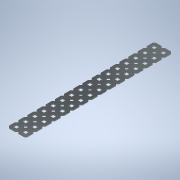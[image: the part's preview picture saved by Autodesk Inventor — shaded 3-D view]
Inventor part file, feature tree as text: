
AUTODESK INVENTOR PART (.ipt)
format: ipt  version: 2020 (Build 240168000, 168)  size: 2,255,872 bytes
history: native  units: mm (DEFAULTED — no unit token found)
features: other x125, extrude x125, plane x2, split x2, imported_body x1, pattern_linear x1, sketch x1
ambient origin geometry x8: Origin, YZ Plane, XZ Plane, XY Plane, X Axis, Y Axis, Z Axis, Center Point
bodies: Solid1 (feature_tree)
feature tree (257):
  imported_body  "Base1"
  pattern_linear  "Rectangular Pattern1"  Spacing1=0.0mm  [1 undecoded]
  plane  "Work Plane1"
  split  "Split1"
  plane  "Work Plane2"
  split  "Split2"
  sketch  "Sketch1"  dims[d1=1.1684mm d2=0.0mm d3=250.0mm d5=12.7mm d6=50.0mm d8=12.7mm d9=0.0mm d10=0.0mm d11=0.0mm d12=0.0mm d13=0.0mm d14=0.0mm d15=0.0mm d16=0.0mm d17=0.0mm d18=0.0mm d19=0.0mm d20=0.0mm d21=0.0mm d22=0.0mm d23=0.0mm d24=0.0mm d25=0.0mm d26=0.0mm d27=0.0mm d28=0.0mm d29=0.0mm d30=0.0mm d31=0.0mm d32=0.0mm d33=0.0mm d34=0.0mm d35=0.0mm d36=0.0mm d37=0.0mm d38=0.0mm d39=0.0mm d40=0.0mm d41=0.0mm d42=0.0mm d43=0.0mm d44=0.0mm d45=0.0mm d46=0.0mm d47=0.0mm d48=0.0mm d49=0.0mm d50=0.0mm d51=0.0mm d52=0.0mm d53=0.0mm d54=0.0mm d55=0.0mm d56=0.0mm d57=0.0mm d58=0.0mm d59=0.0mm d60=0.0mm d61=0.0mm d62=0.0mm d63=0.0mm d64=0.0mm d65=0.0mm d66=0.0mm d67=0.0mm d68=0.0mm d69=0.0mm d70=0.0mm d71=0.0mm d72=0.0mm d73=0.0mm d74=0.0mm d75=0.0mm d76=0.0mm d77=0.0mm d78=0.0mm d79=0.0mm d80=0.0mm d81=0.0mm d82=0.0mm d83=0.0mm d84=0.0mm d85=0.0mm d86=0.0mm d87=0.0mm d88=0.0mm d89=0.0mm d90=0.0mm d91=0.0mm d92=0.0mm d93=0.0mm d94=0.0mm d95=0.0mm d96=0.0mm d97=0.0mm d98=0.0mm d99=0.0mm d100=0.0mm d101=0.0mm d102=0.0mm d103=0.0mm d104=0.0mm d105=0.0mm d106=0.0mm d107=0.0mm d108=0.0mm d109=0.0mm d110=0.0mm d111=0.0mm d112=0.0mm d113=0.0mm d114=0.0mm d115=0.0mm d116=0.0mm d117=0.0mm d118=0.0mm d119=0.0mm d120=0.0mm d121=0.0mm d122=0.0mm d123=0.0mm d124=0.0mm d125=0.0mm d126=0.0mm d127=0.0mm d128=0.0mm d129=0.0mm d130=0.0mm d131=0.0mm d132=0.0mm d133=0.0mm d134=0.0mm d135=0.0mm d136=0.0mm d137=0.0mm d138=0.0mm d139=0.0mm d140=0.0mm d141=0.0mm d142=0.0mm d143=0.0mm d144=0.0mm d145=0.0mm d146=0.0mm d147=0.0mm d148=0.0mm d149=0.0mm d150=0.0mm d151=0.0mm d152=0.0mm d153=0.0mm d154=0.0mm d155=0.0mm d156=0.0mm d157=0.0mm d158=0.0mm d159=0.0mm d160=0.0mm d161=0.0mm d162=0.0mm d163=0.0mm d164=0.0mm d165=0.0mm d166=0.0mm d167=0.0mm d168=0.0mm d169=0.0mm d170=0.0mm d171=0.0mm d172=0.0mm d173=0.0mm d174=0.0mm d175=0.0mm d176=0.0mm d177=0.0mm d178=0.0mm d179=0.0mm d180=0.0mm d181=0.0mm d182=0.0mm d183=0.0mm d184=0.0mm d185=0.0mm d186=0.0mm d187=0.0mm d188=0.0mm d189=0.0mm d190=0.0mm d191=0.0mm d192=0.0mm d193=0.0mm d194=0.0mm d195=0.0mm d196=0.0mm d197=0.0mm d198=0.0mm d199=0.0mm d200=0.0mm d201=0.0mm d202=0.0mm d203=0.0mm d204=0.0mm d205=0.0mm d206=0.0mm d207=0.0mm d208=0.0mm d209=0.0mm d210=0.0mm d211=0.0mm d212=0.0mm d213=0.0mm d214=0.0mm d215=0.0mm d216=0.0mm d217=0.0mm d218=0.0mm d219=0.0mm d220=0.0mm d221=0.0mm d222=0.0mm d223=0.0mm d224=0.0mm d225=0.0mm d226=0.0mm d227=0.0mm d228=0.0mm d229=0.0mm d230=0.0mm d231=0.0mm d232=0.0mm d233=0.0mm d234=0.0mm d235=0.0mm d236=0.0mm d237=0.0mm d238=0.0mm d239=0.0mm d240=0.0mm d241=0.0mm d242=0.0mm d243=0.0mm d244=0.0mm d245=0.0mm d246=0.0mm d247=0.0mm d248=0.0mm d249=0.0mm d250=0.0mm d251=0.0mm d252=0.0mm d253=0.0mm d254=0.0mm d255=0.0mm d256=0.0mm d257=0.0mm d258=0.0mm]
  other  "Srf1"
  other  "Srf2"
  other  "Srf3"
  other  "Srf4"
  other  "Srf5"
  other  "Srf6"
  other  "Srf7"
  other  "Srf8"
  other  "Srf9"
  other  "Srf10"
  other  "Srf11"
  other  "Srf12"
  other  "Srf13"
  other  "Srf14"
  other  "Srf15"
  other  "Srf16"
  other  "Srf17"
  other  "Srf18"
  other  "Srf19"
  other  "Srf20"
  other  "Srf21"
  other  "Srf22"
  other  "Srf23"
  other  "Srf24"
  other  "Srf25"
  other  "Srf26"
  other  "Srf27"
  other  "Srf28"
  other  "Srf29"
  other  "Srf30"
  other  "Srf31"
  other  "Srf32"
  other  "Srf33"
  other  "Srf34"
  other  "Srf35"
  other  "Srf36"
  other  "Srf37"
  other  "Srf38"
  other  "Srf39"
  other  "Srf40"
  other  "Srf41"
  other  "Srf42"
  other  "Srf43"
  other  "Srf44"
  other  "Srf45"
  other  "Srf46"
  other  "Srf47"
  other  "Srf48"
  other  "Srf49"
  other  "Srf50"
  other  "Srf51"
  other  "Srf52"
  other  "Srf53"
  other  "Srf54"
  other  "Srf55"
  other  "Srf56"
  other  "Srf57"
  other  "Srf58"
  other  "Srf59"
  other  "Srf60"
  other  "Srf61"
  other  "Srf62"
  other  "Srf63"
  other  "Srf64"
  other  "Srf65"
  other  "Srf66"
  other  "Srf67"
  other  "Srf68"
  other  "Srf69"
  other  "Srf70"
  other  "Srf71"
  other  "Srf72"
  other  "Srf73"
  other  "Srf74"
  other  "Srf75"
  other  "Srf76"
  other  "Srf77"
  other  "Srf78"
  other  "Srf79"
  other  "Srf80"
  other  "Srf81"
  other  "Srf82"
  other  "Srf83"
  other  "Srf84"
  other  "Srf85"
  other  "Srf86"
  other  "Srf87"
  other  "Srf88"
  other  "Srf89"
  other  "Srf90"
  other  "Srf91"
  other  "Srf92"
  other  "Srf93"
  other  "Srf94"
  other  "Srf95"
  other  "Srf96"
  other  "Srf97"
  other  "Srf98"
  other  "Srf99"
  other  "Srf100"
  other  "Srf101"
  other  "Srf102"
  other  "Srf103"
  other  "Srf104"
  other  "Srf105"
  other  "Srf106"
  other  "Srf107"
  other  "Srf108"
  other  "Srf109"
  other  "Srf110"
  other  "Srf111"
  other  "Srf112"
  other  "Srf113"
  other  "Srf114"
  other  "Srf115"
  other  "Srf116"
  other  "Srf117"
  other  "Srf118"
  other  "Srf119"
  other  "Srf120"
  other  "Srf121"
  other  "Srf122"
  other  "Srf123"
  other  "Srf124"
  other  "Srf125"
  extrude  "ExtrusionSrf1"  Depth=250.0mm
  extrude  "ExtrusionSrf2"  Depth=12.7mm
  extrude  "ExtrusionSrf3"  Depth=50.0mm
  extrude  "ExtrusionSrf4"  TaperAngle=0.0deg  [1 undecoded]
  extrude  "ExtrusionSrf5"  TaperAngle=0.0deg  [1 undecoded]
  extrude  "ExtrusionSrf6"  TaperAngle=0.0deg  [1 undecoded]
  extrude  "ExtrusionSrf7"  TaperAngle=0.0deg  [1 undecoded]
  extrude  "ExtrusionSrf8"  TaperAngle=0.0deg  [1 undecoded]
  extrude  "ExtrusionSrf9"  TaperAngle=0.0deg  [1 undecoded]
  extrude  "ExtrusionSrf10"  TaperAngle=0.0deg  [1 undecoded]
  extrude  "ExtrusionSrf11"  TaperAngle=0.0deg  [1 undecoded]
  extrude  "ExtrusionSrf12"  TaperAngle=0.0deg  [1 undecoded]
  extrude  "ExtrusionSrf13"  TaperAngle=0.0deg  [1 undecoded]
  extrude  "ExtrusionSrf14"  TaperAngle=0.0deg  [1 undecoded]
  extrude  "ExtrusionSrf15"  TaperAngle=0.0deg  [1 undecoded]
  extrude  "ExtrusionSrf16"  TaperAngle=0.0deg  [1 undecoded]
  extrude  "ExtrusionSrf17"  TaperAngle=0.0deg  [1 undecoded]
  extrude  "ExtrusionSrf18"  TaperAngle=0.0deg  [1 undecoded]
  extrude  "ExtrusionSrf19"  TaperAngle=0.0deg  [1 undecoded]
  extrude  "ExtrusionSrf20"  TaperAngle=0.0deg  [1 undecoded]
  extrude  "ExtrusionSrf21"  TaperAngle=0.0deg  [1 undecoded]
  extrude  "ExtrusionSrf22"  TaperAngle=0.0deg  [1 undecoded]
  extrude  "ExtrusionSrf23"  TaperAngle=0.0deg  [1 undecoded]
  extrude  "ExtrusionSrf24"  TaperAngle=0.0deg  [1 undecoded]
  extrude  "ExtrusionSrf25"  TaperAngle=0.0deg  [1 undecoded]
  extrude  "ExtrusionSrf26"  TaperAngle=0.0deg  [1 undecoded]
  extrude  "ExtrusionSrf27"  TaperAngle=0.0deg  [1 undecoded]
  extrude  "ExtrusionSrf28"  TaperAngle=0.0deg  [1 undecoded]
  extrude  "ExtrusionSrf29"  TaperAngle=0.0deg  [1 undecoded]
  extrude  "ExtrusionSrf30"  TaperAngle=0.0deg  [1 undecoded]
  extrude  "ExtrusionSrf31"  TaperAngle=0.0deg  [1 undecoded]
  extrude  "ExtrusionSrf32"  TaperAngle=0.0deg  [1 undecoded]
  extrude  "ExtrusionSrf33"  TaperAngle=0.0deg  [1 undecoded]
  extrude  "ExtrusionSrf34"  TaperAngle=0.0deg  [1 undecoded]
  extrude  "ExtrusionSrf35"  TaperAngle=0.0deg  [1 undecoded]
  extrude  "ExtrusionSrf36"  TaperAngle=0.0deg  [1 undecoded]
  extrude  "ExtrusionSrf37"  TaperAngle=0.0deg  [1 undecoded]
  extrude  "ExtrusionSrf38"  TaperAngle=0.0deg  [1 undecoded]
  extrude  "ExtrusionSrf39"  TaperAngle=0.0deg  [1 undecoded]
  extrude  "ExtrusionSrf40"  TaperAngle=0.0deg  [1 undecoded]
  extrude  "ExtrusionSrf41"  TaperAngle=0.0deg  [1 undecoded]
  extrude  "ExtrusionSrf42"  TaperAngle=0.0deg  [1 undecoded]
  extrude  "ExtrusionSrf43"  TaperAngle=0.0deg  [1 undecoded]
  extrude  "ExtrusionSrf44"  TaperAngle=0.0deg  [1 undecoded]
  extrude  "ExtrusionSrf45"  TaperAngle=0.0deg  [1 undecoded]
  extrude  "ExtrusionSrf46"  TaperAngle=0.0deg  [1 undecoded]
  extrude  "ExtrusionSrf47"  TaperAngle=0.0deg  [1 undecoded]
  extrude  "ExtrusionSrf48"  TaperAngle=0.0deg  [1 undecoded]
  extrude  "ExtrusionSrf49"  TaperAngle=0.0deg  [1 undecoded]
  extrude  "ExtrusionSrf50"  TaperAngle=0.0deg  [1 undecoded]
  extrude  "ExtrusionSrf51"  TaperAngle=0.0deg  [1 undecoded]
  extrude  "ExtrusionSrf52"  TaperAngle=0.0deg  [1 undecoded]
  extrude  "ExtrusionSrf53"  TaperAngle=0.0deg  [1 undecoded]
  extrude  "ExtrusionSrf54"  TaperAngle=0.0deg  [1 undecoded]
  extrude  "ExtrusionSrf55"  TaperAngle=0.0deg  [1 undecoded]
  extrude  "ExtrusionSrf56"  TaperAngle=0.0deg  [1 undecoded]
  extrude  "ExtrusionSrf57"  TaperAngle=0.0deg  [1 undecoded]
  extrude  "ExtrusionSrf58"  TaperAngle=0.0deg  [1 undecoded]
  extrude  "ExtrusionSrf59"  TaperAngle=0.0deg  [1 undecoded]
  extrude  "ExtrusionSrf60"  TaperAngle=0.0deg  [1 undecoded]
  extrude  "ExtrusionSrf61"  TaperAngle=0.0deg  [1 undecoded]
  extrude  "ExtrusionSrf62"  TaperAngle=0.0deg  [1 undecoded]
  extrude  "ExtrusionSrf63"  TaperAngle=0.0deg  [1 undecoded]
  extrude  "ExtrusionSrf64"  TaperAngle=0.0deg  [1 undecoded]
  extrude  "ExtrusionSrf65"  TaperAngle=0.0deg  [1 undecoded]
  extrude  "ExtrusionSrf66"  TaperAngle=0.0deg  [1 undecoded]
  extrude  "ExtrusionSrf67"  TaperAngle=0.0deg  [1 undecoded]
  extrude  "ExtrusionSrf68"  TaperAngle=0.0deg  [1 undecoded]
  extrude  "ExtrusionSrf69"  TaperAngle=0.0deg  [1 undecoded]
  extrude  "ExtrusionSrf70"  TaperAngle=0.0deg  [1 undecoded]
  extrude  "ExtrusionSrf71"  TaperAngle=0.0deg  [1 undecoded]
  extrude  "ExtrusionSrf72"  TaperAngle=0.0deg  [1 undecoded]
  extrude  "ExtrusionSrf73"  TaperAngle=0.0deg  [1 undecoded]
  extrude  "ExtrusionSrf74"  TaperAngle=0.0deg  [1 undecoded]
  extrude  "ExtrusionSrf75"  TaperAngle=0.0deg  [1 undecoded]
  extrude  "ExtrusionSrf76"  TaperAngle=0.0deg  [1 undecoded]
  extrude  "ExtrusionSrf77"  TaperAngle=0.0deg  [1 undecoded]
  extrude  "ExtrusionSrf78"  TaperAngle=0.0deg  [1 undecoded]
  extrude  "ExtrusionSrf79"  TaperAngle=0.0deg  [1 undecoded]
  extrude  "ExtrusionSrf80"  TaperAngle=0.0deg  [1 undecoded]
  extrude  "ExtrusionSrf81"  TaperAngle=0.0deg  [1 undecoded]
  extrude  "ExtrusionSrf82"  TaperAngle=0.0deg  [1 undecoded]
  extrude  "ExtrusionSrf83"  TaperAngle=0.0deg  [1 undecoded]
  extrude  "ExtrusionSrf84"  TaperAngle=0.0deg  [1 undecoded]
  extrude  "ExtrusionSrf85"  TaperAngle=0.0deg  [1 undecoded]
  extrude  "ExtrusionSrf86"  TaperAngle=0.0deg  [1 undecoded]
  extrude  "ExtrusionSrf87"  TaperAngle=0.0deg  [1 undecoded]
  extrude  "ExtrusionSrf88"  TaperAngle=0.0deg  [1 undecoded]
  extrude  "ExtrusionSrf89"  TaperAngle=0.0deg  [1 undecoded]
  extrude  "ExtrusionSrf90"  TaperAngle=0.0deg  [1 undecoded]
  extrude  "ExtrusionSrf91"  TaperAngle=0.0deg  [1 undecoded]
  extrude  "ExtrusionSrf92"  TaperAngle=0.0deg  [1 undecoded]
  extrude  "ExtrusionSrf93"  TaperAngle=0.0deg  [1 undecoded]
  extrude  "ExtrusionSrf94"  TaperAngle=0.0deg  [1 undecoded]
  extrude  "ExtrusionSrf95"  TaperAngle=0.0deg  [1 undecoded]
  extrude  "ExtrusionSrf96"  TaperAngle=0.0deg  [1 undecoded]
  extrude  "ExtrusionSrf97"  TaperAngle=0.0deg  [1 undecoded]
  extrude  "ExtrusionSrf98"  TaperAngle=0.0deg  [1 undecoded]
  extrude  "ExtrusionSrf99"  TaperAngle=0.0deg  [1 undecoded]
  extrude  "ExtrusionSrf100"  TaperAngle=0.0deg  [1 undecoded]
  extrude  "ExtrusionSrf101"  TaperAngle=0.0deg  [1 undecoded]
  extrude  "ExtrusionSrf102"  TaperAngle=0.0deg  [1 undecoded]
  extrude  "ExtrusionSrf103"  TaperAngle=0.0deg  [1 undecoded]
  extrude  "ExtrusionSrf104"  TaperAngle=0.0deg  [1 undecoded]
  extrude  "ExtrusionSrf105"  TaperAngle=0.0deg  [1 undecoded]
  extrude  "ExtrusionSrf106"  TaperAngle=0.0deg  [1 undecoded]
  extrude  "ExtrusionSrf107"  TaperAngle=0.0deg  [1 undecoded]
  extrude  "ExtrusionSrf108"  TaperAngle=0.0deg  [1 undecoded]
  extrude  "ExtrusionSrf109"  TaperAngle=0.0deg  [1 undecoded]
  extrude  "ExtrusionSrf110"  TaperAngle=0.0deg  [1 undecoded]
  extrude  "ExtrusionSrf111"  TaperAngle=0.0deg  [1 undecoded]
  extrude  "ExtrusionSrf112"  TaperAngle=0.0deg  [1 undecoded]
  extrude  "ExtrusionSrf113"  TaperAngle=0.0deg  [1 undecoded]
  extrude  "ExtrusionSrf114"  TaperAngle=0.0deg  [1 undecoded]
  extrude  "ExtrusionSrf115"  TaperAngle=0.0deg  [1 undecoded]
  extrude  "ExtrusionSrf116"  TaperAngle=0.0deg  [1 undecoded]
  extrude  "ExtrusionSrf117"  TaperAngle=0.0deg  [1 undecoded]
  extrude  "ExtrusionSrf118"  TaperAngle=0.0deg  [1 undecoded]
  extrude  "ExtrusionSrf119"  TaperAngle=0.0deg  [1 undecoded]
  extrude  "ExtrusionSrf120"  TaperAngle=0.0deg  [1 undecoded]
  extrude  "ExtrusionSrf121"  TaperAngle=0.0deg  [1 undecoded]
  extrude  "ExtrusionSrf122"  TaperAngle=0.0deg  [1 undecoded]
  extrude  "ExtrusionSrf123"  TaperAngle=0.0deg  [1 undecoded]
  extrude  "ExtrusionSrf124"  TaperAngle=0.0deg  [1 undecoded]
  extrude  "ExtrusionSrf125"  TaperAngle=0.0deg  [1 undecoded]
note: 123 required parameter values undecoded (feature->parameter linkage not recoverable at this tier; creation-order binding heuristic only, values carry confidence <= 0.55)
